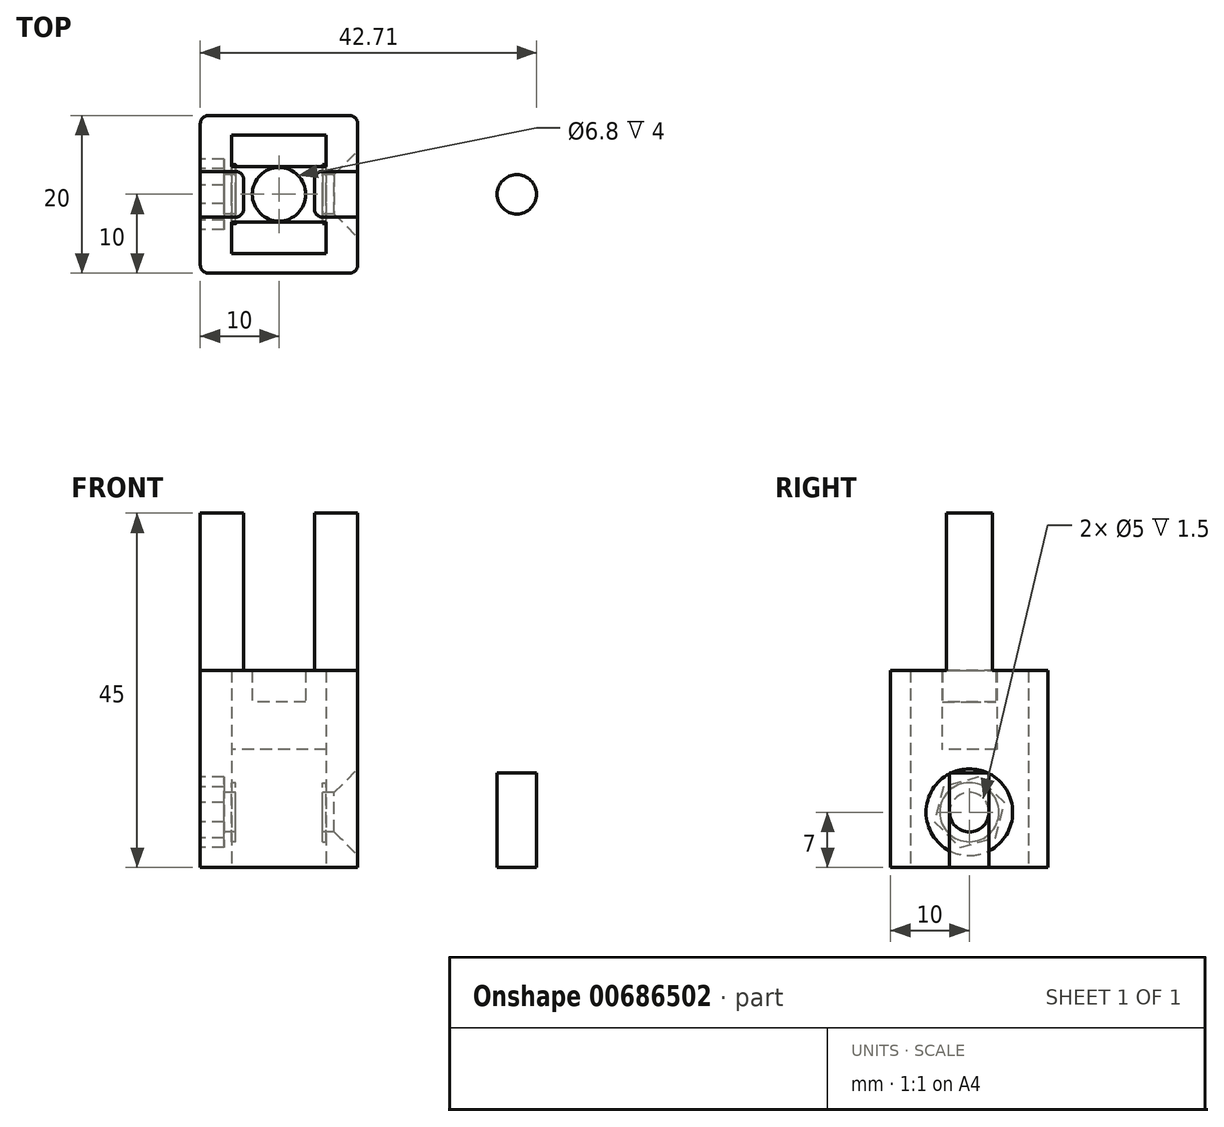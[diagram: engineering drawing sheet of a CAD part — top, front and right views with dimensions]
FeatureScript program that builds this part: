
annotation { "Feature Type Name" : "Feature", "Feature Type Description" : "" }
export const myFeature = defineFeature(function(context is Context, id is Id, definition is map)
    precondition{}
    {
        {
            var Q0;
            Q0=qCreatedBy(makeId("Top.planeOp"),FACE);
            var sketch = newSketch(context, id + "F0", { "sketchPlane" : qUnion([Q0])});
            skLineSegment(sketch, "E0.bottom", {"start": v(-10, 10) * mm, "end": v(10, 10) * mm});
            skLineSegment(sketch, "E0.top", {"start": v(-10, -10) * mm, "end": v(10, -10) * mm});
            skLineSegment(sketch, "E0.left", {"start": v(-10, 10) * mm, "end": v(-10, -10) * mm});
            skLineSegment(sketch, "E0.right", {"start": v(10, 10) * mm, "end": v(10, -10) * mm});
            skCircle(sketch, "E1", {"center": v(0, 0) * mm, "radius": 3.4 * mm});
            skSolve(sketch);
        }
        {
            var Q0;
            Q0=makeQuery(id+"F0.imprint","IMPRINT",FACE,{"disambiguationData":[TD([[makeQuery(id+"F0.imprint","IMPRINT",EDGE,{"derivedFrom":sQuery(id+"F0.wireOp",EDGE,"E0.bottom")}),-1.0]])]});
            extrude(context, id + "F1", {"entities" : qUnion([Q0]), "depth" : 25 * mm, "offsetDistance" : 25 * mm});
        }
        {
            var Q0;
            Q0=makeQuery(id+"F0.imprint","IMPRINT",FACE,{"disambiguationData":[TD([[makeQuery(id+"F0.imprint","IMPRINT",EDGE,{"derivedFrom":sQuery(id+"F0.wireOp",EDGE,"E1")}),1.0]])]});
            extrude(context, id + "F2", {"entities" : qUnion([Q0]), "operationType" : NewBodyOperationType.ADD, "depth" : 21 * mm, "offsetDistance" : 25 * mm});
        }
        {
            var Q0;
            Q0=makeQuery(id+"F0.imprint","IMPRINT",FACE,{"disambiguationData":[TD([[makeQuery(id+"F0.imprint","IMPRINT",EDGE,{"derivedFrom":sQuery(id+"F0.wireOp",EDGE,"E0.bottom")}),-1.0]])]});
            var sketch = newSketch(context, id + "F3", { "sketchPlane" : qUnion([Q0])});
            skLineSegment(sketch, "E2.bottom", {"start": v(-6, 7.5) * mm, "end": v(6, 7.5) * mm});
            skLineSegment(sketch, "E2.top", {"start": v(-6, -7.5) * mm, "end": v(6, -7.5) * mm});
            skLineSegment(sketch, "E2.left", {"start": v(-6, 7.5) * mm, "end": v(-6, -7.5) * mm});
            skLineSegment(sketch, "E2.right", {"start": v(6, 7.5) * mm, "end": v(6, -7.5) * mm});
            skSolve(sketch);
        }
        {
            var Q0;
            Q0=makeQuery(id+"F3.imprint","IMPRINT",FACE,{"disambiguationData":[TD([[makeQuery(id+"F3.imprint","IMPRINT",EDGE,{"derivedFrom":sQuery(id+"F3.wireOp",EDGE,"E2.bottom")}),-1.0]])]});
            var Q1;
            Q1=makeQuery(id+"F3.imprint","IMPRINT",FACE,{"disambiguationData":[TD([[makeQuery(id+"F3.imprint","IMPRINT",EDGE,{"derivedFrom":makeQuery(id+"F0.imprint","IMPRINT",EDGE,{"derivedFrom":sQuery(id+"F0.wireOp",EDGE,"E1")})}),1.0]])]});
            extrude(context, id + "F4", {"entities" : qUnion([Q0, Q1]), "operationType" : NewBodyOperationType.REMOVE, "depth" : 15 * mm, "offsetDistance" : 25 * mm});
        }
        {
            var Q0;
            Q0=makeQuery(id+"F4.boolean.opBoolean","COPY",FACE,{"derivedFrom":makeQuery(id+"F4.opExtrude","SWEPT_FACE",FACE,{"disambiguationData":[OSD([sQuery(id+"F3.wireOp",EDGE,"E2.right")])]})});
            var sketch = newSketch(context, id + "F5", { "sketchPlane" : qUnion([Q0])});
            skCircle(sketch, "E3", {"center": v(0, 7) * mm, "radius": 2.5 * mm});
            skCircle(sketch, "E4", {"center": v(0, 7) * mm, "radius": 7 * mm});
            skSolve(sketch);
        }
        {
            var Q0;
            {var subQ0=sQuery(id+"F5.wireOp",EDGE,"E3");var subQ1=makeQuery(id+"F4.boolean.opBoolean","COPY",EDGE,{"derivedFrom":makeQuery(id+"F4.opExtrude","CAP_EDGE",EDGE,{"disambiguationData":[OSD([sQuery(id+"F3.wireOp",EDGE,"E2.top")])],"isStart":true})});var subQ2=makeQuery(id+"F5.imprint","INTERSECT",VERTEX,{"disambiguationData":[OD(0.0)],"derivedFrom":[subQ1,subQ0]});Q0=makeQuery(id+"F5.imprint","IMPRINT",FACE,{"disambiguationData":[TD([[makeQuery(id+"F5.imprint","IMPRINT",EDGE,{"disambiguationData":[TD([[subQ2,1.0]])],"derivedFrom":subQ0}),1.0]])]});}
            var Q1;
            {var subQ0=sQuery(id+"F5.wireOp",EDGE,"E3");var subQ1=makeQuery(id+"F4.boolean.opBoolean","COPY",EDGE,{"derivedFrom":makeQuery(id+"F4.opExtrude","CAP_EDGE",EDGE,{"disambiguationData":[OSD([sQuery(id+"F3.wireOp",EDGE,"E2.top")])],"isStart":true})});var subQ2=makeQuery(id+"F5.imprint","INTERSECT",VERTEX,{"disambiguationData":[OD(0.0)],"derivedFrom":[subQ1,subQ0]});Q1=makeQuery(id+"F5.imprint","IMPRINT",FACE,{"disambiguationData":[TD([[makeQuery(id+"F5.imprint","IMPRINT",EDGE,{"disambiguationData":[TD([[subQ2,-1.0]])],"derivedFrom":subQ0}),1.0]])]});}
            var Q2;
            Q2=makeQuery(id+"F5.imprint","IMPRINT",FACE,{"disambiguationData":[TD([[makeQuery(id+"F5.imprint","IMPRINT",EDGE,{"derivedFrom":sQuery(id+"F5.wireOp",EDGE,"E3")}),1.0]])]});
            extrude(context, id + "F6", {"entities" : qUnion([Q0, Q1, Q2]), "operationType" : NewBodyOperationType.REMOVE, "oppositeDirection" : true, "depth" : 5 * mm, "offsetDistance" : 25 * mm, "hasSecondDirection" : true, "secondDirectionOppositeDirection" : false, "secondDirectionDepth" : 20 * mm});
        }
        {
            var Q0;
            Q0=makeQuery(id+"F4.boolean.opBoolean","COPY",FACE,{"derivedFrom":makeQuery(id+"F4.opExtrude","CAP_FACE",FACE,{"disambiguationData":[OSD([sQuery(id+"F3.wireOp",EDGE,"E2.bottom"),sQuery(id+"F3.wireOp",EDGE,"E2.top"),sQuery(id+"F3.wireOp",EDGE,"E2.left"),sQuery(id+"F3.wireOp",EDGE,"E2.right")])],"isStart":false})});
            var sketch = newSketch(context, id + "F7", { "sketchPlane" : qUnion([Q0])});
            skLineSegment(sketch, "E5.bottom", {"start": v(6, 7.5) * mm, "end": v(-6, 7.5) * mm});
            skLineSegment(sketch, "E5.top", {"start": v(6, 3.5) * mm, "end": v(-6, 3.5) * mm});
            skLineSegment(sketch, "E5.left", {"start": v(6, 7.5) * mm, "end": v(6, 3.5) * mm});
            skLineSegment(sketch, "E5.right", {"start": v(-6, 7.5) * mm, "end": v(-6, 3.5) * mm});
            skLineSegment(sketch, "E6.bottom", {"start": v(6, -7.5) * mm, "end": v(-6, -7.5) * mm});
            skLineSegment(sketch, "E6.top", {"start": v(6, -3.5) * mm, "end": v(-6, -3.5) * mm});
            skLineSegment(sketch, "E6.left", {"start": v(6, -7.5) * mm, "end": v(6, -3.5) * mm});
            skLineSegment(sketch, "E6.right", {"start": v(-6, -7.5) * mm, "end": v(-6, -3.5) * mm});
            skSolve(sketch);
        }
        {
            var Q0;
            Q0=makeQuery(id+"F7.imprint","IMPRINT",FACE,{"disambiguationData":[TD([[makeQuery(id+"F7.imprint","IMPRINT",EDGE,{"derivedFrom":sQuery(id+"F7.wireOp",EDGE,"E5.bottom")}),-1.0]])]});
            var Q1;
            Q1=makeQuery(id+"F7.imprint","IMPRINT",FACE,{"disambiguationData":[TD([[makeQuery(id+"F7.imprint","IMPRINT",EDGE,{"derivedFrom":sQuery(id+"F7.wireOp",EDGE,"E6.bottom")}),1.0]])]});
            extrude(context, id + "F8", {"entities" : qUnion([Q0, Q1]), "operationType" : NewBodyOperationType.REMOVE, "oppositeDirection" : true, "depth" : 25 * mm, "offsetDistance" : 25 * mm});
        }
        {
            var Q0;
            Q0=makeQuery(id+"F1.opExtrude","CAP_FACE",FACE,{"disambiguationData":[OSD([sQuery(id+"F0.wireOp",EDGE,"E0.bottom"),sQuery(id+"F0.wireOp",EDGE,"E0.top"),sQuery(id+"F0.wireOp",EDGE,"E0.left"),sQuery(id+"F0.wireOp",EDGE,"E0.right"),sQuery(id+"F0.wireOp",EDGE,"E1")])],"isStart":false});
            var sketch = newSketch(context, id + "F9", { "sketchPlane" : qUnion([Q0])});
            skLineSegment(sketch, "E7.bottom", {"start": v(10, -2.9) * mm, "end": v(4.5, -2.9) * mm});
            skLineSegment(sketch, "E7.top", {"start": v(10, 2.9) * mm, "end": v(4.5, 2.9) * mm});
            skLineSegment(sketch, "E7.left", {"start": v(10, -2.9) * mm, "end": v(10, 2.9) * mm});
            skLineSegment(sketch, "E7.right", {"start": v(4.5, -2.9) * mm, "end": v(4.5, 2.9) * mm});
            skLineSegment(sketch, "E8.bottom", {"start": v(-10, -2.9) * mm, "end": v(-4.5, -2.9) * mm});
            skLineSegment(sketch, "E8.top", {"start": v(-10, 2.9) * mm, "end": v(-4.5, 2.9) * mm});
            skLineSegment(sketch, "E8.left", {"start": v(-10, -2.9) * mm, "end": v(-10, 2.9) * mm});
            skLineSegment(sketch, "E8.right", {"start": v(-4.5, -2.9) * mm, "end": v(-4.5, 2.9) * mm});
            skSolve(sketch);
        }
        {
            var Q0;
            Q0=makeQuery(id+"F9.imprint","IMPRINT",FACE,{"disambiguationData":[TD([[makeQuery(id+"F9.imprint","IMPRINT",EDGE,{"derivedFrom":sQuery(id+"F9.wireOp",EDGE,"E7.bottom")}),-1.0]])]});
            var Q1;
            Q1=makeQuery(id+"F9.imprint","IMPRINT",FACE,{"disambiguationData":[TD([[makeQuery(id+"F9.imprint","IMPRINT",EDGE,{"derivedFrom":sQuery(id+"F9.wireOp",EDGE,"E8.bottom")}),1.0]])]});
            extrude(context, id + "F10", {"entities" : qUnion([Q0, Q1]), "operationType" : NewBodyOperationType.ADD, "depth" : 20 * mm, "offsetDistance" : 25 * mm});
        }
        {
            var Q0;
            Q0=makeQuery(id+"F1.opExtrude","SWEPT_EDGE",EDGE,{"disambiguationData":[OSD([sQuery(id+"F0.wireOp",EDGE,"E0.top"),sQuery(id+"F0.wireOp",EDGE,"E0.right")])]});
            var Q1;
            Q1=makeQuery(id+"F1.opExtrude","SWEPT_EDGE",EDGE,{"disambiguationData":[OSD([sQuery(id+"F0.wireOp",EDGE,"E0.bottom"),sQuery(id+"F0.wireOp",EDGE,"E0.right")])]});
            var Q2;
            Q2=makeQuery(id+"F1.opExtrude","SWEPT_EDGE",EDGE,{"disambiguationData":[OSD([sQuery(id+"F0.wireOp",EDGE,"E0.bottom"),sQuery(id+"F0.wireOp",EDGE,"E0.left")])]});
            var Q3;
            Q3=makeQuery(id+"F1.opExtrude","SWEPT_EDGE",EDGE,{"disambiguationData":[OSD([sQuery(id+"F0.wireOp",EDGE,"E0.top"),sQuery(id+"F0.wireOp",EDGE,"E0.left")])]});
            var Q4;
            Q4=makeQuery(id+"F10.opExtrude","SWEPT_EDGE",EDGE,{"disambiguationData":[OSD([sQuery(id+"F9.wireOp",EDGE,"E8.bottom"),sQuery(id+"F9.wireOp",EDGE,"E8.right")])]});
            var Q5;
            Q5=makeQuery(id+"F10.opExtrude","SWEPT_EDGE",EDGE,{"disambiguationData":[OSD([sQuery(id+"F9.wireOp",EDGE,"E8.top"),sQuery(id+"F9.wireOp",EDGE,"E8.right")])]});
            var Q6;
            Q6=makeQuery(id+"F10.opExtrude","SWEPT_EDGE",EDGE,{"disambiguationData":[OSD([sQuery(id+"F9.wireOp",EDGE,"E7.top"),sQuery(id+"F9.wireOp",EDGE,"E7.right")])]});
            var Q7;
            Q7=makeQuery(id+"F10.opExtrude","SWEPT_EDGE",EDGE,{"disambiguationData":[OSD([sQuery(id+"F9.wireOp",EDGE,"E7.bottom"),sQuery(id+"F9.wireOp",EDGE,"E7.right")])]});
            var Q8;
            Q8=makeQuery(id+"F8.boolean.opBoolean","COPY",EDGE,{"derivedFrom":makeQuery(id+"F8.opExtrude","CAP_EDGE",EDGE,{"disambiguationData":[OSD([sQuery(id+"F7.wireOp",EDGE,"E5.top")])],"isStart":true})});
            var Q9;
            Q9=makeQuery(id+"F8.boolean.opBoolean","COPY",EDGE,{"derivedFrom":makeQuery(id+"F8.opExtrude","CAP_EDGE",EDGE,{"disambiguationData":[OSD([sQuery(id+"F7.wireOp",EDGE,"E6.top")])],"isStart":true})});
            fillet(context, id + "F11", {"entities" : qUnion([Q0, Q1, Q2, Q3, Q4, Q5, Q6, Q7, Q8, Q9]), "radius" : 1 * mm, "tangentPropagation" : true, "allowEdgeOverflow" : false});
        }
        {
            var Q0;
            Q0=qCreatedBy(makeId("Top.planeOp"),FACE);
            var sketch = newSketch(context, id + "F12", { "sketchPlane" : qUnion([Q0])});
            skCircle(sketch, "E9", {"center": v(30.2, 0) * mm, "radius": 2.5 * mm});
            skSolve(sketch);
        }
        {
            var Q0;
            Q0=makeQuery(id+"F12.imprint","IMPRINT",FACE,{"disambiguationData":[TD([[makeQuery(id+"F12.imprint","IMPRINT",EDGE,{"derivedFrom":sQuery(id+"F12.wireOp",EDGE,"E9")}),1.0]])]});
            extrude(context, id + "F13", {"entities" : qUnion([Q0]), "depth" : 12 * mm, "offsetDistance" : 25 * mm});
        }
        {
            var Q0;
            Q0=makeQuery(id+"F10.boolean.opBoolean","MERGE",FACE,{"derivedFrom":[makeQuery(id+"F1.opExtrude","SWEPT_FACE",FACE,{"disambiguationData":[OSD([sQuery(id+"F0.wireOp",EDGE,"E0.left")])]}),makeQuery(id+"F10.opExtrude","SWEPT_FACE",FACE,{"disambiguationData":[OSD([sQuery(id+"F9.wireOp",EDGE,"E8.left")])]})]});
            var sketch = newSketch(context, id + "F14", { "sketchPlane" : qUnion([Q0])});
            skCircle(sketch, "E10.cCircle", {"center": v(0, 7) * mm, "radius": 4 * mm, "construction": true});
            skLineSegment(sketch, "E10.0", {"start": v(-4.45, 8.22) * mm, "end": v(-1.17, 11.47) * mm});
            skLineSegment(sketch, "E10.1", {"start": v(-1.17, 11.47) * mm, "end": v(3.28, 10.25) * mm});
            skLineSegment(sketch, "E10.2", {"start": v(3.28, 10.25) * mm, "end": v(4.45, 5.78) * mm});
            skLineSegment(sketch, "E10.3", {"start": v(4.45, 5.78) * mm, "end": v(1.17, 2.53) * mm});
            skLineSegment(sketch, "E10.4", {"start": v(1.17, 2.53) * mm, "end": v(-3.28, 3.75) * mm});
            skLineSegment(sketch, "E10.5", {"start": v(-3.28, 3.75) * mm, "end": v(-4.45, 8.22) * mm});
            skPoint(sketch, "E10.0.midPoint", {"position": v(-2.81, 9.84) * mm});
            skSolve(sketch);
        }
        {
            var Q0;
            Q0=makeQuery(id+"F14.imprint","IMPRINT",FACE,{"disambiguationData":[TD([[makeQuery(id+"F14.imprint","IMPRINT",EDGE,{"derivedFrom":sQuery(id+"F14.wireOp",EDGE,"E10.0")}),-1.0]])]});
            extrude(context, id + "F15", {"entities" : qUnion([Q0]), "operationType" : NewBodyOperationType.REMOVE, "oppositeDirection" : true, "depth" : 3 * mm, "offsetDistance" : 25 * mm});
        }
        {
            var Q0;
            Q0=makeQuery(id+"F6.boolean.opBoolean","INTERSECT",EDGE,{"derivedFrom":[makeQuery(id+"F1.opExtrude","SWEPT_FACE",FACE,{"disambiguationData":[OSD([sQuery(id+"F0.wireOp",EDGE,"E0.right")])]}),makeQuery(id+"F6.opExtrude","SWEPT_FACE",FACE,{"disambiguationData":[OSD([sQuery(id+"F5.wireOp",EDGE,"E3")])]})]});
            chamfer(context, id + "F16", {"entities" : qUnion([Q0]), "width" : 3 * mm, "tangentPropagation" : true});
        }
        {
            var Q0;
            Q0=makeQuery(id+"F8.boolean.opBoolean","MERGE",FACE,{"derivedFrom":[makeQuery(id+"F4.boolean.opBoolean","COPY",FACE,{"derivedFrom":makeQuery(id+"F4.opExtrude","SWEPT_FACE",FACE,{"disambiguationData":[OSD([sQuery(id+"F3.wireOp",EDGE,"E2.left")])]})}),makeQuery(id+"F8.opExtrude","SWEPT_FACE",FACE,{"disambiguationData":[OSD([sQuery(id+"F7.wireOp",EDGE,"E5.right")])]}),makeQuery(id+"F8.opExtrude","SWEPT_FACE",FACE,{"disambiguationData":[OSD([sQuery(id+"F7.wireOp",EDGE,"E6.right")])]})]});
            var sketch = newSketch(context, id + "F17", { "sketchPlane" : qUnion([Q0])});
            skCircle(sketch, "E11", {"center": v(0, 7) * mm, "radius": 3.75 * mm});
            skSolve(sketch);
        }
        {
            var Q0;
            Q0=makeQuery(id+"F17.imprint","IMPRINT",FACE,{"disambiguationData":[TD([[makeQuery(id+"F17.imprint","IMPRINT",EDGE,{"derivedFrom":sQuery(id+"F17.wireOp",EDGE,"E11")}),1.0]])]});
            extrude(context, id + "F18", {"entities" : qUnion([Q0]), "operationType" : NewBodyOperationType.ADD, "depth" : 0.5 * mm, "offsetDistance" : 25 * mm});
        }
        {
            var Q0;
            Q0=makeQuery(id+"F8.boolean.opBoolean","MERGE",FACE,{"derivedFrom":[makeQuery(id+"F4.boolean.opBoolean","COPY",FACE,{"derivedFrom":makeQuery(id+"F4.opExtrude","SWEPT_FACE",FACE,{"disambiguationData":[OSD([sQuery(id+"F3.wireOp",EDGE,"E2.right")])]})}),makeQuery(id+"F8.opExtrude","SWEPT_FACE",FACE,{"disambiguationData":[OSD([sQuery(id+"F7.wireOp",EDGE,"E5.left")])]}),makeQuery(id+"F8.opExtrude","SWEPT_FACE",FACE,{"disambiguationData":[OSD([sQuery(id+"F7.wireOp",EDGE,"E6.left")])]})]});
            var sketch = newSketch(context, id + "F19", { "sketchPlane" : qUnion([Q0])});
            skCircle(sketch, "E12", {"center": v(0, 7) * mm, "radius": 3.75 * mm});
            skSolve(sketch);
        }
        {
            var Q0;
            Q0=makeQuery(id+"F19.imprint","IMPRINT",FACE,{"disambiguationData":[TD([[makeQuery(id+"F19.imprint","IMPRINT",EDGE,{"derivedFrom":sQuery(id+"F19.wireOp",EDGE,"E12")}),1.0]])]});
            extrude(context, id + "F20", {"entities" : qUnion([Q0]), "operationType" : NewBodyOperationType.ADD, "depth" : .5 * mm, "offsetDistance" : 25 * mm});
        }
    });
